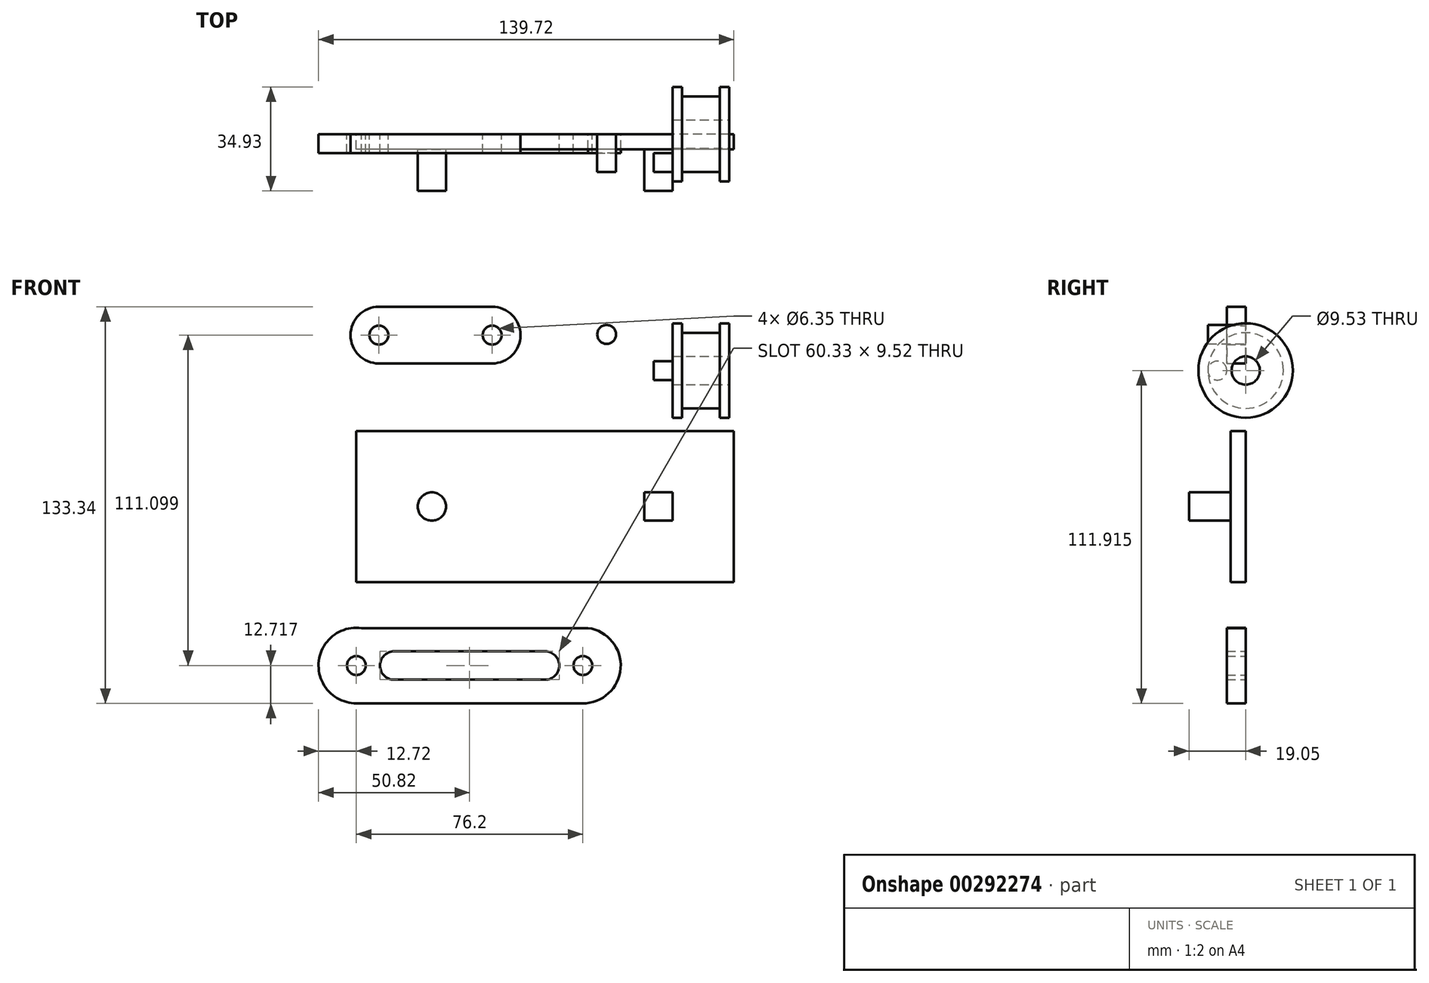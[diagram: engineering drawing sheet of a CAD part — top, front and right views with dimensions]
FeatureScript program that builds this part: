
annotation { "Feature Type Name" : "Feature", "Feature Type Description" : "" }
export const myFeature = defineFeature(function(context is Context, id is Id, definition is map)
    precondition{}
    {
        {
            var Q0;
            Q0=qCreatedBy(makeId("Front.planeOp"),FACE);
            var sketch = newSketch(context, id + "F0", { "sketchPlane" : qUnion([Q0])});
            skLineSegment(sketch, "E0.bottom", {"start": v(63.5, -25.4) * mm, "end": v(-63.5, -25.4) * mm});
            skLineSegment(sketch, "E0.top", {"start": v(63.5, 25.4) * mm, "end": v(-63.5, 25.4) * mm});
            skLineSegment(sketch, "E0.left", {"start": v(63.5, -25.4) * mm, "end": v(63.5, 25.4) * mm});
            skLineSegment(sketch, "E0.right", {"start": v(-63.5, -25.4) * mm, "end": v(-63.5, 25.4) * mm});
            skPoint(sketch, "E0.middle", {"position": v(0, 0) * mm});
            skCircle(sketch, "E1", {"center": v(-38.1, 0) * mm, "radius": 4.76 * mm});
            skPoint(sketch, "E2.endSnap0", {"position": v(63.5, 0) * mm});
            skLineSegment(sketch, "E3.bottom", {"start": v(33.34, 4.76) * mm, "end": v(42.86, 4.76) * mm});
            skLineSegment(sketch, "E3.top", {"start": v(33.34, -4.76) * mm, "end": v(42.86, -4.76) * mm});
            skLineSegment(sketch, "E3.left", {"start": v(33.34, 4.76) * mm, "end": v(33.34, -4.76) * mm});
            skLineSegment(sketch, "E3.right", {"start": v(42.86, 4.76) * mm, "end": v(42.86, -4.76) * mm});
            skPoint(sketch, "E3.middle", {"position": v(38.1, 0) * mm});
            skSolve(sketch);
        }
        {
            var Q0;
            Q0=makeQuery(id+"F0.imprint","IMPRINT",FACE,{"disambiguationData":[TD([[makeQuery(id+"F0.imprint","IMPRINT",EDGE,{"derivedFrom":sQuery(id+"F0.wireOp",EDGE,"E3.bottom")}),-1.0]])]});
            extrude(context, id + "F1", {"entities" : qUnion([Q0]), "depth" : 19.05 * mm});
        }
        {
            var Q0;
            Q0=makeQuery(id+"F0.imprint","IMPRINT",FACE,{"disambiguationData":[TD([[makeQuery(id+"F0.imprint","IMPRINT",EDGE,{"derivedFrom":sQuery(id+"F0.wireOp",EDGE,"E0.bottom")}),-1.0]])]});
            extrude(context, id + "F2", {"entities" : qUnion([Q0]), "operationType" : NewBodyOperationType.ADD, "depth" : 5.08 * mm});
        }
        {
            var Q0;
            Q0=qCreatedBy(makeId("Front.planeOp"),FACE);
            var sketch = newSketch(context, id + "F3", { "sketchPlane" : qUnion([Q0])});
            skCircle(sketch, "E4", {"center": v(-17.82, 57.63) * mm, "radius": 3.18 * mm});
            skCircle(sketch, "E5", {"center": v(-55.92, 57.63) * mm, "radius": 3.17 * mm});
            skArc(sketch, "E6", {"start": v(-17.82, 48.1) * mm, "mid": v(-8.3, 57.63) * mm, "end": v(-17.82, 67.15) * mm});
            skArc(sketch, "E7", {"start": v(-55.92, 48.1) * mm, "mid": v(-65.45, 57.63) * mm, "end": v(-55.92, 67.15) * mm});
            skLineSegment(sketch, "E8", {"start": v(-55.92, 67.15) * mm, "end": v(-17.82, 67.15) * mm});
            skLineSegment(sketch, "E9", {"start": v(-17.82, 48.1) * mm, "end": v(-55.92, 48.1) * mm});
            skSolve(sketch);
        }
        {
            var Q0;
            Q0=makeQuery(id+"F3.imprint","IMPRINT",FACE,{"disambiguationData":[TD([[makeQuery(id+"F3.imprint","IMPRINT",EDGE,{"derivedFrom":sQuery(id+"F3.wireOp",EDGE,"E4")}),-1.0]])]});
            extrude(context, id + "F4", {"entities" : qUnion([Q0]), "depth" : 6.35 * mm});
        }
        {
            var Q0;
            Q0=qCreatedBy(makeId("Front.planeOp"),FACE);
            var sketch = newSketch(context, id + "F5", { "sketchPlane" : qUnion([Q0])});
            skCircle(sketch, "E10", {"center": v(12.7, -53.47) * mm, "radius": 3.18 * mm});
            skCircle(sketch, "E11", {"center": v(-63.5, -53.47) * mm, "radius": 3.18 * mm});
            skLineSegment(sketch, "E12", {"start": v(-61.8, -40.87) * mm, "end": v(14.4, -40.87) * mm});
            skLineSegment(sketch, "E13", {"start": v(-63.38, -66.2) * mm, "end": v(12.58, -66.2) * mm});
            skArc(sketch, "E14", {"start": v(-61.8, -40.87) * mm, "mid": v(-76.2, -52.68) * mm, "end": v(-63.38, -66.2) * mm});
            skArc(sketch, "E15", {"start": v(14.4, -40.87) * mm, "mid": v(25.38, -54.4) * mm, "end": v(12.58, -66.2) * mm});
            skPoint(sketch, "E16.endSnap0", {"position": v(-25.4, -66.2) * mm});
            skLineSegment(sketch, "E17", {"start": v(-25.4, -48.71) * mm, "end": v(0, -48.71) * mm});
            skLineSegment(sketch, "E18", {"start": v(-25.4, -48.71) * mm, "end": v(-50.8, -48.71) * mm});
            skLineSegment(sketch, "E19", {"start": v(-25.4, -58.24) * mm, "end": v(0, -58.24) * mm});
            skLineSegment(sketch, "E20", {"start": v(-25.4, -58.24) * mm, "end": v(-50.8, -58.24) * mm});
            skArc(sketch, "E21", {"start": v(0, -48.71) * mm, "mid": v(4.76, -53.47) * mm, "end": v(0, -58.24) * mm});
            skArc(sketch, "E22", {"start": v(-50.8, -48.71) * mm, "mid": v(-55.56, -53.47) * mm, "end": v(-50.8, -58.24) * mm});
            skSolve(sketch);
        }
        {
            var Q0;
            Q0=makeQuery(id+"F5.imprint","IMPRINT",FACE,{"disambiguationData":[TD([[makeQuery(id+"F5.imprint","IMPRINT",EDGE,{"derivedFrom":sQuery(id+"F5.wireOp",EDGE,"E10")}),-1.0]])]});
            extrude(context, id + "F6", {"entities" : qUnion([Q0]), "depth" : 6.35 * mm});
        }
        {
            var Q0;
            Q0=qCreatedBy(makeId("Front.planeOp"),FACE);
            var sketch = newSketch(context, id + "F7", { "sketchPlane" : qUnion([Q0])});
            skCircle(sketch, "E23", {"center": v(20.7, 57.87) * mm, "radius": 3.18 * mm});
            skSolve(sketch);
        }
        {
            var Q0;
            Q0=makeQuery(id+"F7.imprint","IMPRINT",FACE,{"disambiguationData":[TD([[makeQuery(id+"F7.imprint","IMPRINT",EDGE,{"derivedFrom":sQuery(id+"F7.wireOp",EDGE,"E23")}),1.0]])]});
            extrude(context, id + "F8", {"entities" : qUnion([Q0]), "depth" : 12.7 * mm});
        }
        {
            var Q0;
            Q0=qCreatedBy(makeId("Front.planeOp"),FACE);
            var sketch = newSketch(context, id + "F9", { "sketchPlane" : qUnion([Q0])});
            skLineSegment(sketch, "E24", {"start": v(46.04, 58.42) * mm, "end": v(58.74, 58.42) * mm});
            skLineSegment(sketch, "E25", {"start": v(58.74, 58.42) * mm, "end": v(58.74, 50.49) * mm});
            skLineSegment(sketch, "E26", {"start": v(46.04, 50.49) * mm, "end": v(46.04, 58.42) * mm});
            skLineSegment(sketch, "E27", {"start": v(58.74, 58.42) * mm, "end": v(58.74, 61.6) * mm});
            skLineSegment(sketch, "E28", {"start": v(58.74, 61.6) * mm, "end": v(61.92, 61.6) * mm});
            skLineSegment(sketch, "E29", {"start": v(61.92, 61.6) * mm, "end": v(61.92, 50.49) * mm});
            skLineSegment(sketch, "E30", {"start": v(42.87, 50.49) * mm, "end": v(42.87, 61.6) * mm});
            skLineSegment(sketch, "E31", {"start": v(42.87, 61.6) * mm, "end": v(46.04, 61.6) * mm});
            skLineSegment(sketch, "E32", {"start": v(46.04, 61.6) * mm, "end": v(46.04, 58.42) * mm});
            skLineSegment(sketch, "E33", {"start": v(61.92, 45.72) * mm, "end": v(30, 45.72) * mm});
            skPoint(sketch, "E33.endSnap0", {"position": v(42.87, 45.72) * mm});
            skLineSegment(sketch, "E34", {"start": v(42.87, 50.49) * mm, "end": v(61.92, 50.49) * mm});
            skSolve(sketch);
        }
        {
            var Q0;
            {var subQ1=sQuery(id+"F9.wireOp",EDGE,"E26");Q0=makeQuery(id+"F9.imprint","IMPRINT",FACE,{"disambiguationData":[TD([[makeQuery(id+"F9.imprint","IMPRINT",EDGE,{"derivedFrom":subQ1}),1.0]])]});}
            var Q1;
            Q1=makeQuery(id+"F9.imprint","IMPRINT",FACE,{"disambiguationData":[TD([[makeQuery(id+"F9.imprint","IMPRINT",EDGE,{"derivedFrom":sQuery(id+"F9.wireOp",EDGE,"E24")}),-1.0]])]});
            var Q2;
            {var subQ1=sQuery(id+"F9.wireOp",EDGE,"E25");Q2=makeQuery(id+"F9.imprint","IMPRINT",FACE,{"disambiguationData":[TD([[makeQuery(id+"F9.imprint","IMPRINT",EDGE,{"derivedFrom":subQ1}),1.0]])]});}
            var Q3;
            Q3=sQuery(id+"F9.wireOp",EDGE,"E33");
            revolve(context, id + "F10", {"entities" : qUnion([Q0, Q1, Q2]), "axis" : qUnion([Q3]), "revolveType" : RevolveType.FULL});
        }
        {
            var Q0;
            Q0=makeQuery(id+"F10.opRevolve","SWEPT_FACE",FACE,{"disambiguationData":[OSD([sQuery(id+"F9.wireOp",EDGE,"E30")])]});
            var sketch = newSketch(context, id + "F11", { "sketchPlane" : qUnion([Q0])});
            skCircle(sketch, "E35", {"center": v(9.53, 45.72) * mm, "radius": 3.18 * mm});
            skSolve(sketch);
        }
        {
            var Q0;
            Q0=makeQuery(id+"F11.imprint","IMPRINT",FACE,{"disambiguationData":[TD([[makeQuery(id+"F11.imprint","IMPRINT",EDGE,{"derivedFrom":sQuery(id+"F11.wireOp",EDGE,"E35")}),1.0]])]});
            extrude(context, id + "F12", {"entities" : qUnion([Q0]), "operationType" : NewBodyOperationType.ADD, "depth" : 6.35 * mm});
        }
        {
            var Q0;
            Q0=makeQuery(id+"F0.imprint","IMPRINT",FACE,{"disambiguationData":[TD([[makeQuery(id+"F0.imprint","IMPRINT",EDGE,{"derivedFrom":sQuery(id+"F0.wireOp",EDGE,"E1")}),1.0]])]});
            extrude(context, id + "F13", {"entities" : qUnion([Q0]), "operationType" : NewBodyOperationType.ADD, "depth" : 19.05 * mm});
        }
    });
